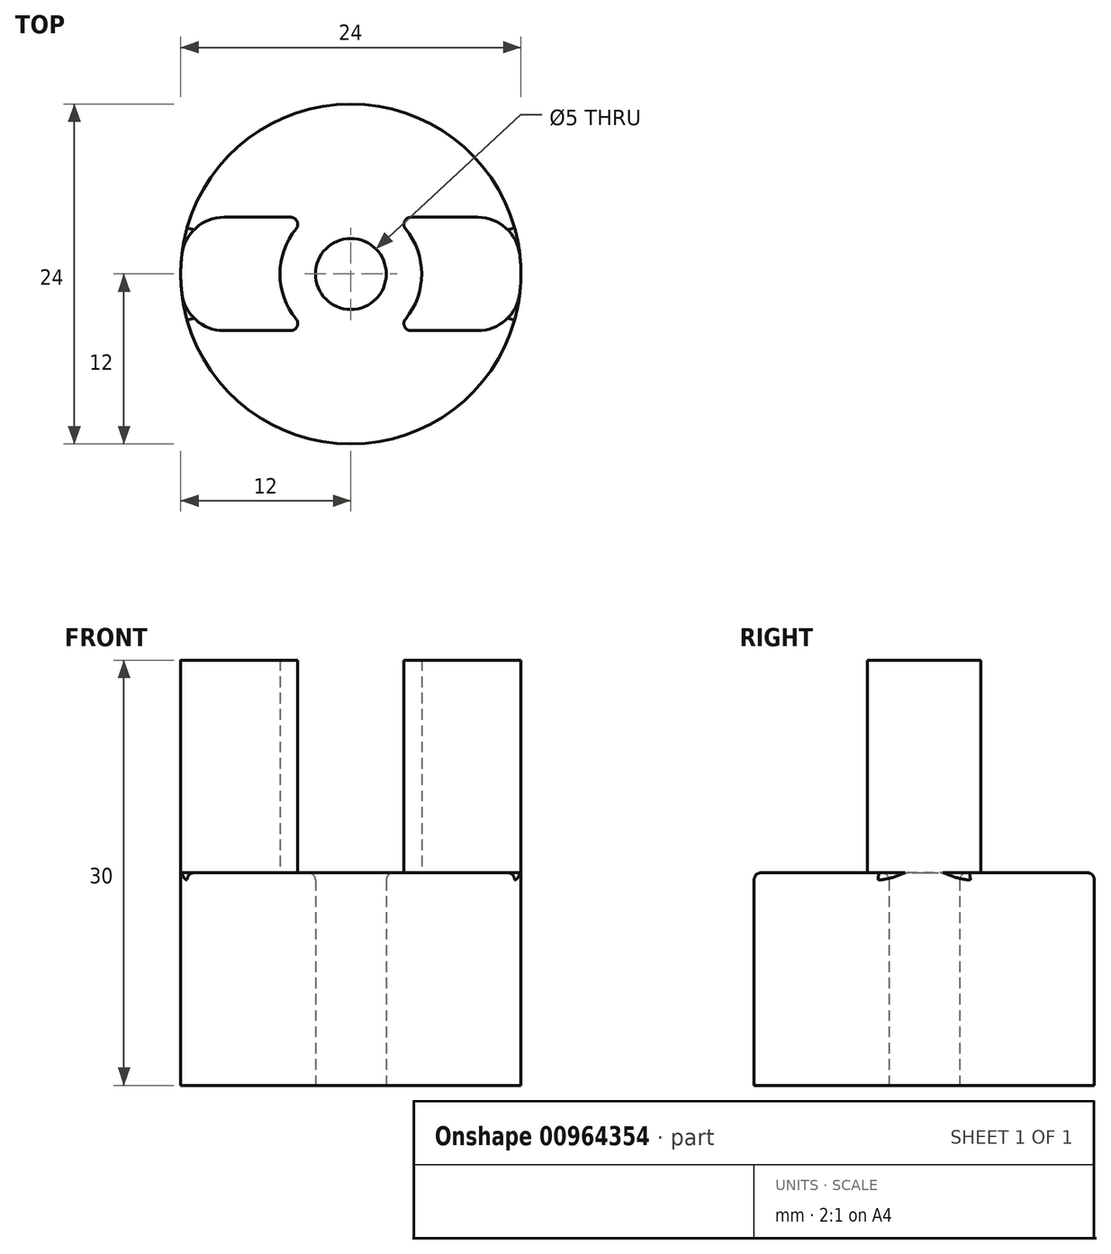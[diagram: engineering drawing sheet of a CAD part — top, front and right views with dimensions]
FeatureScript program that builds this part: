
annotation { "Feature Type Name" : "Feature", "Feature Type Description" : "" }
export const myFeature = defineFeature(function(context is Context, id is Id, definition is map)
    precondition{}
    {
        {
            var Q0;
            Q0=qCreatedBy(makeId("Top.planeOp"),FACE);
            var sketch = newSketch(context, id + "F0", { "sketchPlane" : qUnion([Q0])});
            skCircle(sketch, "E0", {"center": v(0, 0) * mm, "radius": 12 * mm});
            skCircle(sketch, "E1", {"center": v(0, 0) * mm, "radius": 2.5 * mm});
            skSolve(sketch);
        }
        {
            var Q0;
            Q0 = qSketchRegion(id + "F0", true);
            extrude(context, id + "F1", {"entities" : qUnion([Q0]), "depth" : 15 * mm, "offsetDistance" : 25 * mm});
        }
        {
            var Q0;
            Q0=makeQuery(id+"F1.opExtrude","CAP_FACE",FACE,{"disambiguationData":[OSD([sQuery(id+"F0.wireOp",EDGE,"E0"),sQuery(id+"F0.wireOp",EDGE,"E1")])],"isStart":false});
            var sketch = newSketch(context, id + "F2", { "sketchPlane" : qUnion([Q0])});
            skLineSegment(sketch, "E2", {"start": v(-11.31, 4) * mm, "end": v(11.31, 4) * mm});
            skLineSegment(sketch, "E3", {"start": v(-11.31, -4) * mm, "end": v(11.31, -4) * mm});
            skCircle(sketch, "E4", {"center": v(0, 0) * mm, "radius": 5 * mm});
            skCircle(sketch, "E5", {"center": v(0, 0) * mm, "radius": 4 * mm, "construction": true});
            skSolve(sketch);
        }
        {
            var Q0;
            {var subQ0=sQuery(id+"F2.wireOp",EDGE,"E2");var subQ1=makeQuery(id+"F1.opExtrude","CAP_EDGE",EDGE,{"disambiguationData":[OSD([sQuery(id+"F0.wireOp",EDGE,"E0")])],"isStart":false});var subQ2=makeQuery(id+"F2.imprint","INTERSECT",VERTEX,{"disambiguationData":[OD(0.0)],"derivedFrom":[subQ1,subQ0]});Q0=makeQuery(id+"F2.imprint","IMPRINT",FACE,{"disambiguationData":[TD([[makeQuery(id+"F2.imprint","IMPRINT",EDGE,{"disambiguationData":[TD([[subQ2,-1.0]])],"derivedFrom":subQ0}),-1.0]])]});}
            var Q1;
            {var subQ0=sQuery(id+"F2.wireOp",EDGE,"E2");var subQ1=makeQuery(id+"F1.opExtrude","CAP_EDGE",EDGE,{"disambiguationData":[OSD([sQuery(id+"F0.wireOp",EDGE,"E0")])],"isStart":false});var subQ2=makeQuery(id+"F2.imprint","INTERSECT",VERTEX,{"disambiguationData":[OD(1.0)],"derivedFrom":[subQ1,subQ0]});Q1=makeQuery(id+"F2.imprint","IMPRINT",FACE,{"disambiguationData":[TD([[makeQuery(id+"F2.imprint","IMPRINT",EDGE,{"disambiguationData":[TD([[subQ2,1.0]])],"derivedFrom":subQ0}),-1.0]])]});}
            extrude(context, id + "F3", {"entities" : qUnion([Q0, Q1]), "operationType" : NewBodyOperationType.ADD, "depth" : 15 * mm, "offsetDistance" : 25 * mm});
        }
        {
            var Q0;
            {var subQ0=sQuery(id+"F2.wireOp",EDGE,"E2");var subQ1=sQuery(id+"F0.wireOp",EDGE,"E0");Q0=makeQuery(id+"F3.opExtrude","SWEPT_EDGE",EDGE,{"disambiguationData":[OSD([subQ1,subQ0]),TDD([makeQuery(id+"F2.imprint","INTERSECT",VERTEX,{"disambiguationData":[OD(0.0)],"derivedFrom":[makeQuery(id+"F1.opExtrude","CAP_EDGE",EDGE,{"disambiguationData":[OSD([subQ1])],"isStart":false}),subQ0]})])]});}
            var Q1;
            {var subQ0=sQuery(id+"F2.wireOp",EDGE,"E3");var subQ1=sQuery(id+"F0.wireOp",EDGE,"E0");Q1=makeQuery(id+"F3.opExtrude","SWEPT_EDGE",EDGE,{"disambiguationData":[OSD([subQ1,subQ0]),TDD([makeQuery(id+"F2.imprint","INTERSECT",VERTEX,{"disambiguationData":[OD(0.0)],"derivedFrom":[makeQuery(id+"F1.opExtrude","CAP_EDGE",EDGE,{"disambiguationData":[OSD([subQ1])],"isStart":false}),subQ0]})])]});}
            var Q2;
            {var subQ0=sQuery(id+"F2.wireOp",EDGE,"E2");var subQ1=sQuery(id+"F0.wireOp",EDGE,"E0");Q2=makeQuery(id+"F3.opExtrude","SWEPT_EDGE",EDGE,{"disambiguationData":[OSD([subQ1,subQ0]),TDD([makeQuery(id+"F2.imprint","INTERSECT",VERTEX,{"disambiguationData":[OD(1.0)],"derivedFrom":[makeQuery(id+"F1.opExtrude","CAP_EDGE",EDGE,{"disambiguationData":[OSD([subQ1])],"isStart":false}),subQ0]})])]});}
            var Q3;
            {var subQ0=sQuery(id+"F2.wireOp",EDGE,"E3");var subQ1=sQuery(id+"F0.wireOp",EDGE,"E0");Q3=makeQuery(id+"F3.opExtrude","SWEPT_EDGE",EDGE,{"disambiguationData":[OSD([subQ1,subQ0]),TDD([makeQuery(id+"F2.imprint","INTERSECT",VERTEX,{"disambiguationData":[OD(1.0)],"derivedFrom":[makeQuery(id+"F1.opExtrude","CAP_EDGE",EDGE,{"disambiguationData":[OSD([subQ1])],"isStart":false}),subQ0]})])]});}
            fillet(context, id + "F4", {"entities" : qUnion([Q0, Q1, Q2, Q3]), "radius" : 3 * mm, "tangentPropagation" : true, "allowEdgeOverflow" : false});
        }
        {
            var Q0;
            {var subQ0=sQuery(id+"F2.wireOp",EDGE,"E4");var subQ1=sQuery(id+"F2.wireOp",EDGE,"E2");Q0=makeQuery(id+"F3.opExtrude","SWEPT_EDGE",EDGE,{"disambiguationData":[OSD([subQ1,subQ0]),TDD([makeQuery(id+"F2.imprint","INTERSECT",VERTEX,{"disambiguationData":[OD(0.0)],"derivedFrom":[subQ1,subQ0]})])]});}
            var Q1;
            {var subQ0=sQuery(id+"F2.wireOp",EDGE,"E4");var subQ1=sQuery(id+"F2.wireOp",EDGE,"E3");Q1=makeQuery(id+"F3.opExtrude","SWEPT_EDGE",EDGE,{"disambiguationData":[OSD([subQ1,subQ0]),TDD([makeQuery(id+"F2.imprint","INTERSECT",VERTEX,{"disambiguationData":[OD(0.0)],"derivedFrom":[subQ1,subQ0]})])]});}
            var Q2;
            {var subQ0=sQuery(id+"F2.wireOp",EDGE,"E4");var subQ1=sQuery(id+"F2.wireOp",EDGE,"E2");Q2=makeQuery(id+"F3.opExtrude","SWEPT_EDGE",EDGE,{"disambiguationData":[OSD([subQ1,subQ0]),TDD([makeQuery(id+"F2.imprint","INTERSECT",VERTEX,{"disambiguationData":[OD(1.0)],"derivedFrom":[subQ1,subQ0]})])]});}
            var Q3;
            {var subQ0=sQuery(id+"F2.wireOp",EDGE,"E4");var subQ1=sQuery(id+"F2.wireOp",EDGE,"E3");Q3=makeQuery(id+"F3.opExtrude","SWEPT_EDGE",EDGE,{"disambiguationData":[OSD([subQ1,subQ0]),TDD([makeQuery(id+"F2.imprint","INTERSECT",VERTEX,{"disambiguationData":[OD(1.0)],"derivedFrom":[subQ1,subQ0]})])]});}
            var Q4;
            {var subQ0=sQuery(id+"F2.wireOp",EDGE,"E3");Q4=makeQuery(id+"F3.opExtrude","CAP_EDGE",EDGE,{"disambiguationData":[OSD([subQ0]),TDD([makeQuery(id+"F2.imprint","IMPRINT",EDGE,{"disambiguationData":[TD([[makeQuery(id+"F2.imprint","INTERSECT",VERTEX,{"disambiguationData":[OD(0.0)],"derivedFrom":[makeQuery(id+"F1.opExtrude","CAP_EDGE",EDGE,{"disambiguationData":[OSD([sQuery(id+"F0.wireOp",EDGE,"E0")])],"isStart":false}),subQ0]}),-1.0]])],"derivedFrom":subQ0})])],"isStart":true});}
            var Q5;
            {var subQ0=sQuery(id+"F2.wireOp",EDGE,"E3");Q5=makeQuery(id+"F3.opExtrude","CAP_EDGE",EDGE,{"disambiguationData":[OSD([subQ0]),TDD([makeQuery(id+"F2.imprint","IMPRINT",EDGE,{"disambiguationData":[TD([[makeQuery(id+"F2.imprint","INTERSECT",VERTEX,{"disambiguationData":[OD(1.0)],"derivedFrom":[makeQuery(id+"F1.opExtrude","CAP_EDGE",EDGE,{"disambiguationData":[OSD([sQuery(id+"F0.wireOp",EDGE,"E0")])],"isStart":false}),subQ0]}),1.0]])],"derivedFrom":subQ0})])],"isStart":true});}
            var Q6;
            Q6=makeQuery(id+"F1.opExtrude","CAP_EDGE",EDGE,{"disambiguationData":[OSD([sQuery(id+"F0.wireOp",EDGE,"E1")])],"isStart":false});
            var Q7;
            {var subQ0=sQuery(id+"F2.wireOp",EDGE,"E2");var subQ1=sQuery(id+"F0.wireOp",EDGE,"E0");var subQ2=makeQuery(id+"F1.opExtrude","CAP_EDGE",EDGE,{"disambiguationData":[OSD([subQ1])],"isStart":false});var subQ5=makeQuery(id+"F2.imprint","INTERSECT",VERTEX,{"disambiguationData":[OD(0.0)],"derivedFrom":[subQ2,subQ0]});Q7=makeQuery(id+"F3.boolean.opBoolean","SPLIT",EDGE,{"disambiguationData":[TD([makeQuery(id+"F3.opExtrude","SWEPT_FACE",FACE,{"disambiguationData":[OSD([subQ0]),TDD([makeQuery(id+"F2.imprint","IMPRINT",EDGE,{"disambiguationData":[TD([[subQ5,-1.0]])],"derivedFrom":subQ0})])]})])],"derivedFrom":subQ2});}
            var Q8;
            {var subQ0=sQuery(id+"F2.wireOp",EDGE,"E3");var subQ1=sQuery(id+"F0.wireOp",EDGE,"E0");var subQ2=makeQuery(id+"F1.opExtrude","CAP_EDGE",EDGE,{"disambiguationData":[OSD([subQ1])],"isStart":false});var subQ3=makeQuery(id+"F2.imprint","INTERSECT",VERTEX,{"disambiguationData":[OD(0.0)],"derivedFrom":[subQ2,subQ0]});Q8=makeQuery(id+"F3.boolean.opBoolean","SPLIT",EDGE,{"disambiguationData":[TD([makeQuery(id+"F3.opExtrude","SWEPT_FACE",FACE,{"disambiguationData":[OSD([subQ0]),TDD([makeQuery(id+"F2.imprint","IMPRINT",EDGE,{"disambiguationData":[TD([[subQ3,-1.0]])],"derivedFrom":subQ0})])]})])],"derivedFrom":subQ2});}
            fillet(context, id + "F5", {"entities" : qUnion([Q0, Q1, Q2, Q3, Q4, Q5, Q6, Q7, Q8]), "radius" : .5 * mm, "tangentPropagation" : true, "allowEdgeOverflow" : false});
        }
    });
